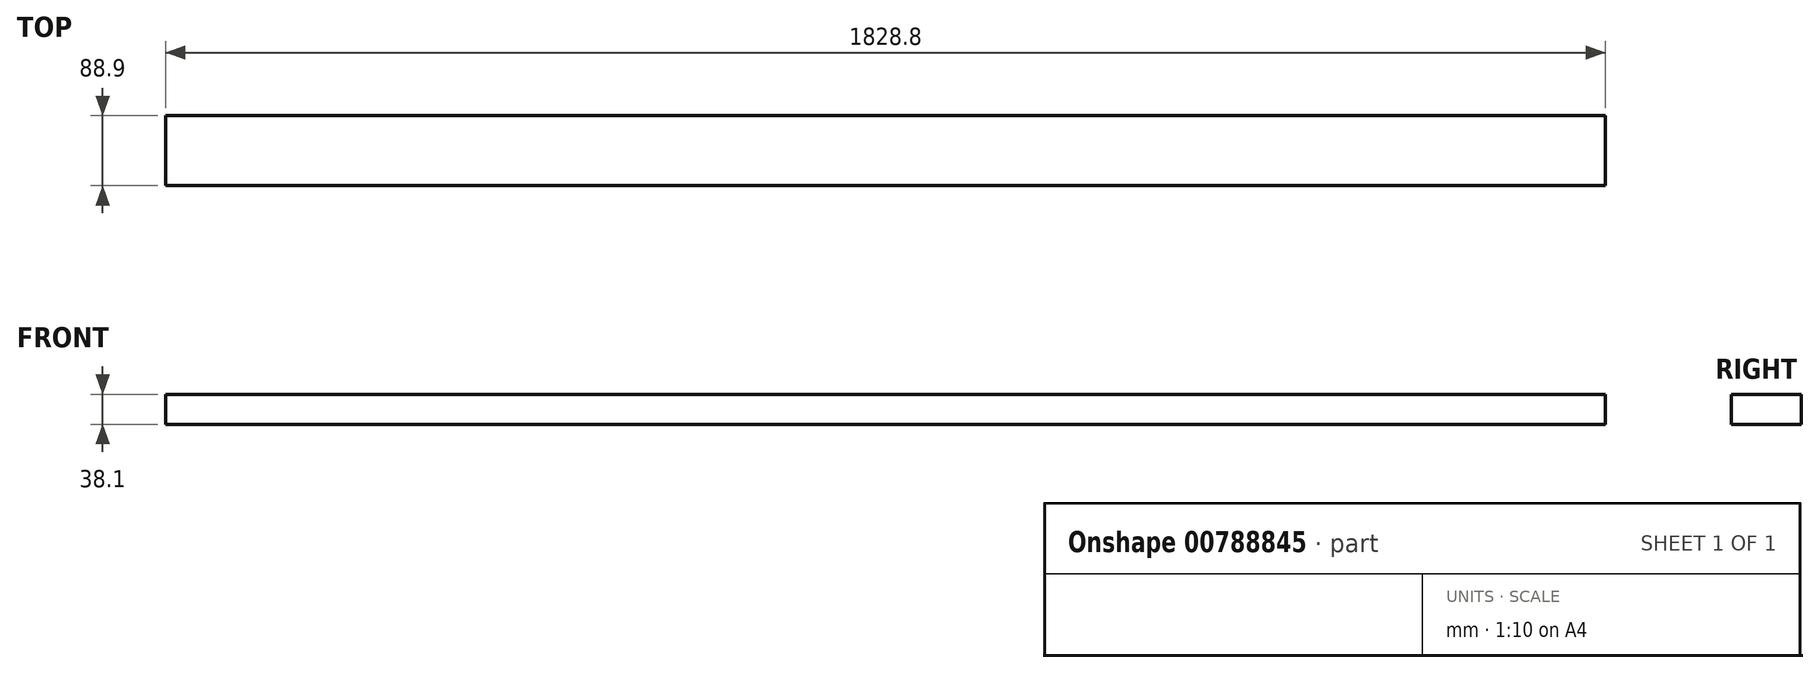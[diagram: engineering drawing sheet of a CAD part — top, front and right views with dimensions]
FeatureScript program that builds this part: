
annotation { "Feature Type Name" : "Feature", "Feature Type Description" : "" }
export const myFeature = defineFeature(function(context is Context, id is Id, definition is map)
    precondition{}
    {
        {
            var Q0;
            Q0=qCreatedBy(makeId("Top.planeOp"),FACE);
            var sketch = newSketch(context, id + "F0", { "sketchPlane" : qUnion([Q0])});
            skLineSegment(sketch, "E0.bottom", {"start": v(-470.92, 88.9) * mm, "end": v(1357.88, 88.9) * mm});
            skLineSegment(sketch, "E0.top", {"start": v(-470.92, 0) * mm, "end": v(1357.88, 0) * mm});
            skLineSegment(sketch, "E0.left", {"start": v(-470.92, 88.9) * mm, "end": v(-470.92, 0) * mm});
            skLineSegment(sketch, "E0.right", {"start": v(1357.88, 88.9) * mm, "end": v(1357.88, 0) * mm});
            skSolve(sketch);
        }
        {
            var Q0;
            Q0=makeQuery(id+"F0.imprint","IMPRINT",FACE,{"disambiguationData":[TD([[makeQuery(id+"F0.imprint","IMPRINT",EDGE,{"derivedFrom":sQuery(id+"F0.wireOp",EDGE,"E0.bottom")}),-1.0]])]});
            extrude(context, id + "F1", {"entities" : qUnion([Q0]), "depth" : 38.1 * mm, "offsetDistance" : 25.4 * mm});
        }
    });
